# Revit family: EV240
name_source: partatom
category: Mechanical Equipment
revit_build: Autodesk Revit 2016 (Build: 20150220_1215(x64)
units: mm (PartAtom-declared; Revit-internal decimal feet)

## family parameters
Always vertical = Yes
Cut with Voids When Loaded = No
Part Type = Normal
Room Calculation Point = No
Round Connector Dimension = Use Diameter
Shared = No
Work Plane-Based = No

## types (1)
- EV240
    Accessories = Backdraft damper 6", 8", Wall cap 6" - white, brown, Wall cap 8" - taupe vinyl, galvanized, paintable galvanneal, Louver with 8" round duct connection - 12" (W) x 8" (H), Percentage timer control (PTL), Push-button point-of-use controls (PBL), PTL Req'd., Percentage timer control with furnace interlock (FM), Electric duct heater - RH series (1-11.5 kW); designed for indoor ductwork installation only
    Controls = Onboard 24VAC transformer/relay package with switched dry contacts
    Description = Energy Recovery Ventilator
    FLA per Motor = 3.3
    Filters = Total qty. 2, MERV 8, spun-polyester media: 10-1/2" x 21-3/4" x 1"
    Hertz = 60
    Manufacturer = Renewaire LLC
    Max. Shipping Dimensions (in carton) = 34" L x 44" W x 34" H
    Max. Shipping Weight (in carton) = 112 lbs.
    Model = EV240
    Motor(s) = Qty. 1, Double-shaft standard motor
    Phase = 1
    Service Area = Renewaire - Interference
    Service Area Visibility = Yes
    Standard Features = White painted cabinet, Line-cord power supply, Low-voltage circuit for controls, Unit may be mounted in any orientation, Cross-core differential pressure ports
    Typical Airflow Range = 100-240 CFM
    URL = www.renewaire.com
    Unit Dimensions = 33-1/2" L x 24" W x 20" H
    Unit Weight = 70 lbs.
    Ventilation Type = Static plate, heat and humidity transfer
    Voltage = 120
    Watts = 216 @ 236 CFM

## geometry (parser evidence)
native form markers: Sweep x2
no freeform markers — native parametric forms only
